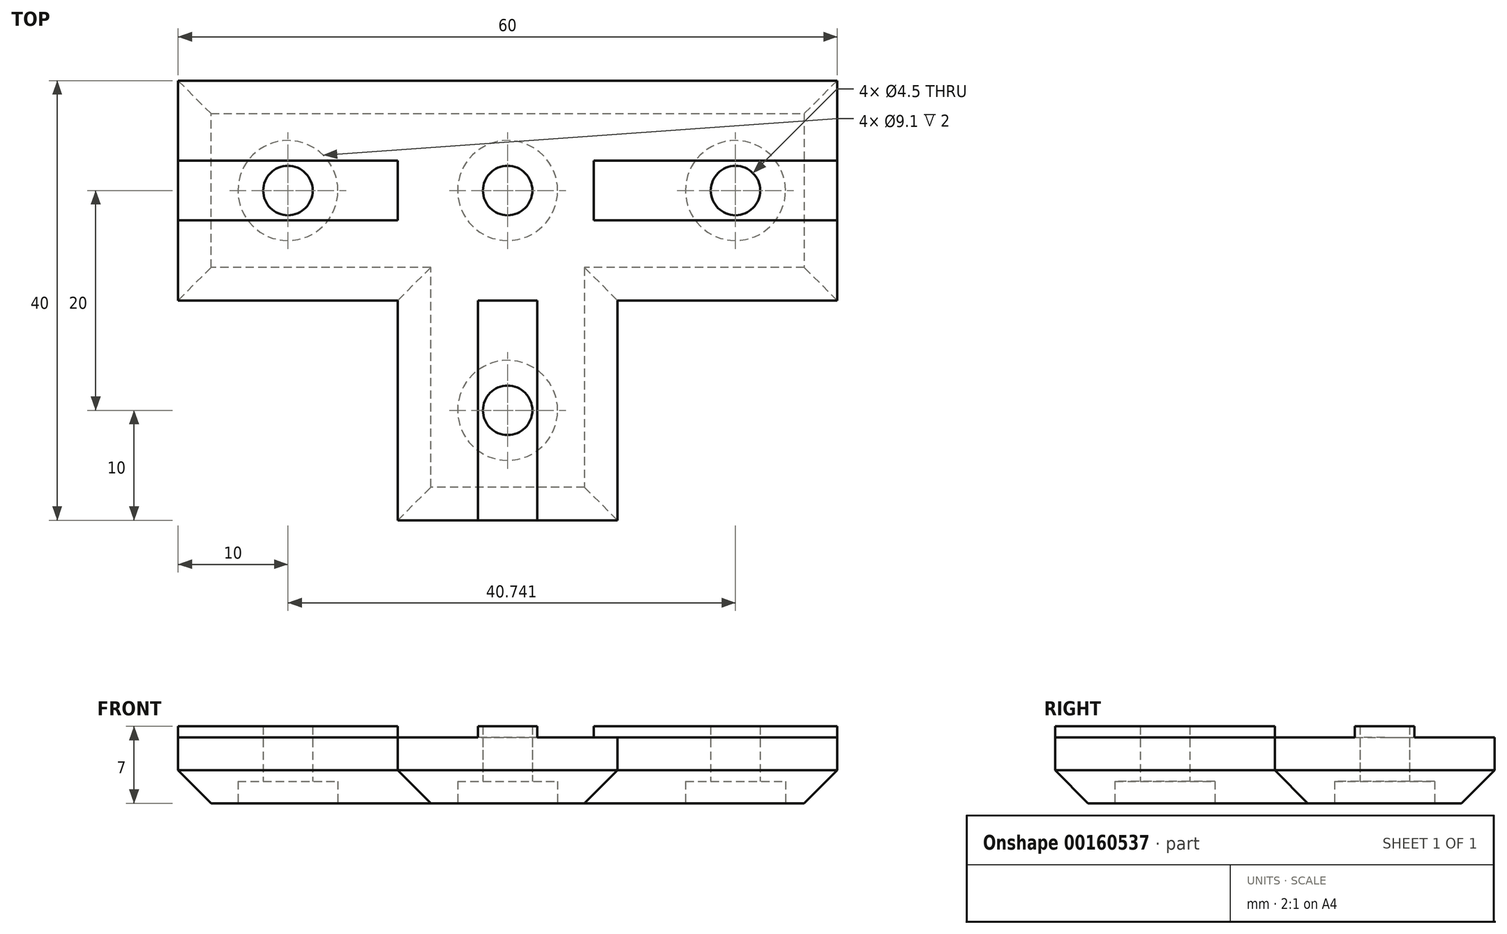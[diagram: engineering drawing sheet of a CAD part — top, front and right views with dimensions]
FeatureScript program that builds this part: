
annotation { "Feature Type Name" : "Feature", "Feature Type Description" : "" }
export const myFeature = defineFeature(function(context is Context, id is Id, definition is map)
    precondition{}
    {
        {
            var Q0;
            Q0=qCreatedBy(makeId("Top.planeOp"),FACE);
            var sketch = newSketch(context, id + "F0", { "sketchPlane" : qUnion([Q0])});
            skLineSegment(sketch, "E0", {"start": v(0, 0) * mm, "end": v(0, 20) * mm, "construction": true});
            skLineSegment(sketch, "E1", {"start": v(0, 0) * mm, "end": v(0, -20) * mm, "construction": true});
            skLineSegment(sketch, "E2", {"start": v(-10, 0) * mm, "end": v(-30, 0) * mm});
            skLineSegment(sketch, "E3", {"start": v(0, 20) * mm, "end": v(-30, 20) * mm});
            skLineSegment(sketch, "E4", {"start": v(-30, 20) * mm, "end": v(-30, 0) * mm});
            skLineSegment(sketch, "E5", {"start": v(0, 20) * mm, "end": v(30, 20) * mm});
            skLineSegment(sketch, "E6", {"start": v(30, 20) * mm, "end": v(30, 0) * mm});
            skLineSegment(sketch, "E7", {"start": v(30, 0) * mm, "end": v(10, 0) * mm});
            skLineSegment(sketch, "E8", {"start": v(0, -20) * mm, "end": v(10, -20) * mm});
            skLineSegment(sketch, "E9", {"start": v(10, -20) * mm, "end": v(10, 0) * mm});
            skLineSegment(sketch, "E10", {"start": v(0, -20) * mm, "end": v(-10, -20) * mm});
            skLineSegment(sketch, "E11", {"start": v(-10, -20) * mm, "end": v(-10, 0) * mm});
            skSolve(sketch);
        }
        {
            var Q0;
            Q0 = qSketchRegion(id + "F0", true);
            extrude(context, id + "F1", {"entities" : qUnion([Q0]), "depth" : 6 * mm});
        }
        {
            var Q0;
            Q0=makeQuery(id+"F1.opExtrude","CAP_FACE",FACE,{"disambiguationData":[OSD([sQuery(id+"F0.wireOp",EDGE,"E2"),sQuery(id+"F0.wireOp",EDGE,"E3"),sQuery(id+"F0.wireOp",EDGE,"E4"),sQuery(id+"F0.wireOp",EDGE,"E5"),sQuery(id+"F0.wireOp",EDGE,"E6"),sQuery(id+"F0.wireOp",EDGE,"E7"),sQuery(id+"F0.wireOp",EDGE,"E8"),sQuery(id+"F0.wireOp",EDGE,"E9"),sQuery(id+"F0.wireOp",EDGE,"E10"),sQuery(id+"F0.wireOp",EDGE,"E11")])],"isStart":false});
            var sketch = newSketch(context, id + "F2", { "sketchPlane" : qUnion([Q0])});
            skLineSegment(sketch, "E12", {"start": v(-30, 10) * mm, "end": v(30, 10) * mm, "construction": true});
            skLineSegment(sketch, "E13", {"start": v(0, -20) * mm, "end": v(0, 0) * mm, "construction": true});
            skLineSegment(sketch, "E14", {"start": v(0, 0) * mm, "end": v(-2.71, 0) * mm});
            skLineSegment(sketch, "E15", {"start": v(-2.71, 0) * mm, "end": v(-2.7, -20) * mm});
            skLineSegment(sketch, "E16", {"start": v(2.71, -20) * mm, "end": v(2.71, 0) * mm});
            skLineSegment(sketch, "E17", {"start": v(2.71, 0) * mm, "end": v(0, 0) * mm});
            skLineSegment(sketch, "E18", {"start": v(-2.7, -20) * mm, "end": v(2.71, -20) * mm});
            skLineSegment(sketch, "E19", {"start": v(7.85, 10) * mm, "end": v(7.85, 12.71) * mm});
            skLineSegment(sketch, "E20", {"start": v(7.85, 12.71) * mm, "end": v(30, 12.71) * mm});
            skLineSegment(sketch, "E21", {"start": v(30, 12.71) * mm, "end": v(30, 7.3) * mm});
            skLineSegment(sketch, "E22", {"start": v(30, 7.3) * mm, "end": v(7.85, 7.29) * mm});
            skLineSegment(sketch, "E23", {"start": v(7.85, 7.29) * mm, "end": v(7.85, 10) * mm});
            skLineSegment(sketch, "E24", {"start": v(-30, 12.71) * mm, "end": v(-30, 7.29) * mm});
            skLineSegment(sketch, "E25", {"start": v(-30, 7.29) * mm, "end": v(-10, 7.29) * mm});
            skLineSegment(sketch, "E26", {"start": v(-10, 7.29) * mm, "end": v(-10, 12.71) * mm});
            skLineSegment(sketch, "E27", {"start": v(-10, 12.71) * mm, "end": v(-30, 12.71) * mm});
            skSolve(sketch);
        }
        {
            var Q0;
            Q0 = qSketchRegion(id + "F2", true);
            extrude(context, id + "F3", {"entities" : qUnion([Q0]), "operationType" : NewBodyOperationType.ADD, "flatOperationType" : FlatOperationType.REMOVE, "offsetDistance" : 25 * mm, "depth" : 1 * mm, "domain" : OperationDomain.MODEL});
        }
        {
            var Q0;
            Q0=makeQuery(id+"F1.opExtrude","CAP_FACE",FACE,{"disambiguationData":[OSD([sQuery(id+"F0.wireOp",EDGE,"E2"),sQuery(id+"F0.wireOp",EDGE,"E3"),sQuery(id+"F0.wireOp",EDGE,"E4"),sQuery(id+"F0.wireOp",EDGE,"E5"),sQuery(id+"F0.wireOp",EDGE,"E6"),sQuery(id+"F0.wireOp",EDGE,"E7"),sQuery(id+"F0.wireOp",EDGE,"E8"),sQuery(id+"F0.wireOp",EDGE,"E9"),sQuery(id+"F0.wireOp",EDGE,"E10"),sQuery(id+"F0.wireOp",EDGE,"E11")])],"isStart":true});
            var sketch = newSketch(context, id + "F4", { "sketchPlane" : qUnion([Q0])});
            skCircle(sketch, "E28", {"center": v(-20, -10) * mm, "radius": 2.25 * mm});
            skCircle(sketch, "E29", {"center": v(0, -10) * mm, "radius": 2.25 * mm});
            skCircle(sketch, "E30", {"center": v(0, 10) * mm, "radius": 2.25 * mm});
            skCircle(sketch, "E31", {"center": v(20.74, -10) * mm, "radius": 2.25 * mm});
            skSolve(sketch);
        }
        {
            var Q0;
            Q0 = qSketchRegion(id + "F4", true);
            extrude(context, id + "F5", {"entities" : qUnion([Q0]), "operationType" : NewBodyOperationType.REMOVE, "endBound" : BoundingType.THROUGH_ALL, "oppositeDirection" : true, "depth" : 25 * mm});
        }
        {
            var Q0;
            Q0=makeQuery(id+"F1.opExtrude","CAP_FACE",FACE,{"disambiguationData":[OSD([sQuery(id+"F0.wireOp",EDGE,"E2"),sQuery(id+"F0.wireOp",EDGE,"E3"),sQuery(id+"F0.wireOp",EDGE,"E4"),sQuery(id+"F0.wireOp",EDGE,"E5"),sQuery(id+"F0.wireOp",EDGE,"E6"),sQuery(id+"F0.wireOp",EDGE,"E7"),sQuery(id+"F0.wireOp",EDGE,"E8"),sQuery(id+"F0.wireOp",EDGE,"E9"),sQuery(id+"F0.wireOp",EDGE,"E10"),sQuery(id+"F0.wireOp",EDGE,"E11")])],"isStart":true});
            var sketch = newSketch(context, id + "F6", { "sketchPlane" : qUnion([Q0])});
            skCircle(sketch, "E32", {"center": v(0, 10) * mm, "radius": 4.55 * mm});
            skCircle(sketch, "E33", {"center": v(0, -10) * mm, "radius": 4.55 * mm});
            skCircle(sketch, "E34", {"center": v(20.74, -10) * mm, "radius": 4.55 * mm});
            skCircle(sketch, "E35", {"center": v(-20, -10) * mm, "radius": 4.55 * mm});
            skSolve(sketch);
        }
        {
            var Q0;
            Q0 = qSketchRegion(id + "F6", true);
            extrude(context, id + "F7", {"entities" : qUnion([Q0]), "operationType" : NewBodyOperationType.REMOVE, "oppositeDirection" : true, "depth" : 2 * mm});
        }
        {
            var Q0;
            Q0=makeQuery(id+"F1.opExtrude","CAP_EDGE",EDGE,{"disambiguationData":[OSD([sQuery(id+"F0.wireOp",EDGE,"E11")])],"isStart":true});
            var Q1;
            Q1=makeQuery(id+"F1.opExtrude","CAP_EDGE",EDGE,{"disambiguationData":[OSD([sQuery(id+"F0.wireOp",EDGE,"E2")])],"isStart":true});
            var Q2;
            Q2=makeQuery(id+"F1.opExtrude","CAP_EDGE",EDGE,{"disambiguationData":[OSD([sQuery(id+"F0.wireOp",EDGE,"E9")])],"isStart":true});
            var Q3;
            Q3=makeQuery(id+"F1.opExtrude","CAP_EDGE",EDGE,{"disambiguationData":[OSD([sQuery(id+"F0.wireOp",EDGE,"E7")])],"isStart":true});
            var Q4;
            Q4=makeQuery(id+"F1.opExtrude","CAP_EDGE",EDGE,{"disambiguationData":[OSD([sQuery(id+"F0.wireOp",EDGE,"E3"),sQuery(id+"F0.wireOp",EDGE,"E5")])],"isStart":true});
            var Q5;
            Q5=makeQuery(id+"F1.opExtrude","CAP_EDGE",EDGE,{"disambiguationData":[OSD([sQuery(id+"F0.wireOp",EDGE,"E6")])],"isStart":true});
            var Q6;
            Q6=makeQuery(id+"F1.opExtrude","CAP_EDGE",EDGE,{"disambiguationData":[OSD([sQuery(id+"F0.wireOp",EDGE,"E4")])],"isStart":true});
            var Q7;
            Q7=makeQuery(id+"F1.opExtrude","CAP_EDGE",EDGE,{"disambiguationData":[OSD([sQuery(id+"F0.wireOp",EDGE,"E8"),sQuery(id+"F0.wireOp",EDGE,"E10")])],"isStart":true});
            chamfer(context, id + "F8", {"entities" : qUnion([Q0, Q1, Q2, Q3, Q4, Q5, Q6, Q7]), "width" : 3 * mm, "tangentPropagation" : true});
        }
    });
